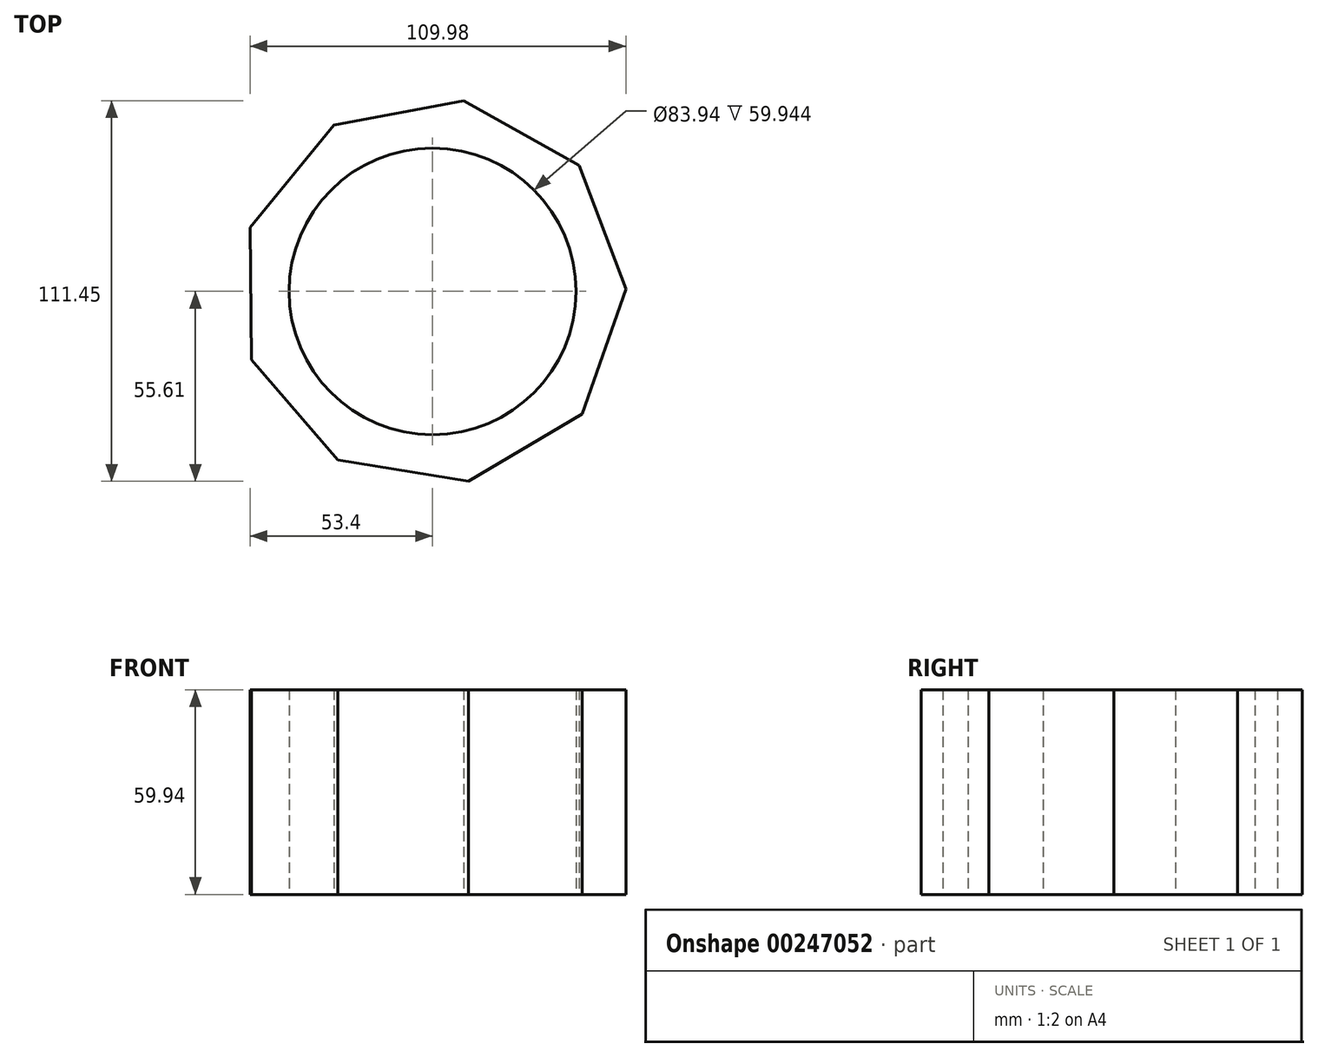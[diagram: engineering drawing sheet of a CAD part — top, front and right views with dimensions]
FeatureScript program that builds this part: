
annotation { "Feature Type Name" : "Feature", "Feature Type Description" : "" }
export const myFeature = defineFeature(function(context is Context, id is Id, definition is map)
    precondition{}
    {
        {
            var Q0;
            Q0=qCreatedBy(makeId("Top.planeOp"),FACE);
            var sketch = newSketch(context, id + "F0", { "sketchPlane" : qUnion([Q0])});
            skCircle(sketch, "E0.cCircle", {"center": v(0, 0) * mm, "radius": 53.17 * mm, "construction": true});
            skLineSegment(sketch, "E0.0", {"start": v(43.77, -35.86) * mm, "end": v(10.48, -55.6) * mm});
            skLineSegment(sketch, "E0.1", {"start": v(10.48, -55.6) * mm, "end": v(-27.71, -49.34) * mm});
            skLineSegment(sketch, "E0.2", {"start": v(-27.71, -49.34) * mm, "end": v(-52.94, -19.98) * mm});
            skLineSegment(sketch, "E0.3", {"start": v(-52.94, -19.98) * mm, "end": v(-53.4, 18.73) * mm});
            skLineSegment(sketch, "E0.4", {"start": v(-53.4, 18.73) * mm, "end": v(-28.87, 48.67) * mm});
            skLineSegment(sketch, "E0.5", {"start": v(-28.87, 48.67) * mm, "end": v(9.17, 55.84) * mm});
            skLineSegment(sketch, "E0.6", {"start": v(9.17, 55.84) * mm, "end": v(42.92, 36.88) * mm});
            skLineSegment(sketch, "E0.7", {"start": v(42.92, 36.88) * mm, "end": v(56.58, 0.67) * mm});
            skLineSegment(sketch, "E0.8", {"start": v(56.58, 0.67) * mm, "end": v(43.77, -35.86) * mm});
            skPoint(sketch, "E0.0.midPoint", {"position": v(27.13, -45.73) * mm});
            skSolve(sketch);
        }
        {
            var Q0;
            Q0 = qSketchRegion(id + "F0", true);
            extrude(context, id + "F1", {"entities" : qUnion([Q0]), "depth" : 59.94 * mm});
        }
        {
            var Q0;
            Q0=qCreatedBy(makeId("Top.planeOp"),FACE);
            var sketch = newSketch(context, id + "F2", { "sketchPlane" : qUnion([Q0])});
            skCircle(sketch, "E1", {"center": v(0, 0) * mm, "radius": 41.97 * mm});
            skSolve(sketch);
        }
        {
            var Q0;
            Q0 = qSketchRegion(id + "F2", true);
            extrude(context, id + "F3", {"entities" : qUnion([Q0]), "operationType" : NewBodyOperationType.REMOVE, "depth" : 83.57 * mm});
        }
    });
